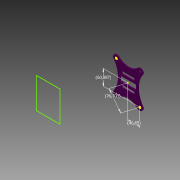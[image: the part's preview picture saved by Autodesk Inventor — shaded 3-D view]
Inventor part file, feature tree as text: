
AUTODESK INVENTOR PART (.ipt)
format: ipt  version: 2015 (Build 190159000, 159)  size: 212,480 bytes
history: native  units: mm
features: sketch x3, extrude x2
ambient origin geometry x8: Origin, YZ Plane, XZ Plane, XY Plane, X Axis, Y Axis, Z Axis, Center Point
bodies: Body1 (feature_tree)
feature tree (5):
  extrude  "Extrusion7"  Depth=3.5mm
  extrude  "Extrusion8"  Depth=4.625mm
  sketch  "Sketch11"  dims[d96=3.5mm d97=3.5mm d98=8.5mm d100=3.5mm d105=3.5mm d106=3.5mm d107=3.5mm d108=3.5mm d109=3.5mm d110=0.0mm d116=10.0mm d117=0.0mm d120=46.987914mm d121=10.941512mm d122=76.703333mm d123=60.886624mm d124=46.65mm]
  sketch  "Sketch1"  dims[d19=46.65mm d72=0.0mm d93=3.5mm]
  sketch  "Sketch8"  dims[d94=37.55mm d95=4.625mm]
